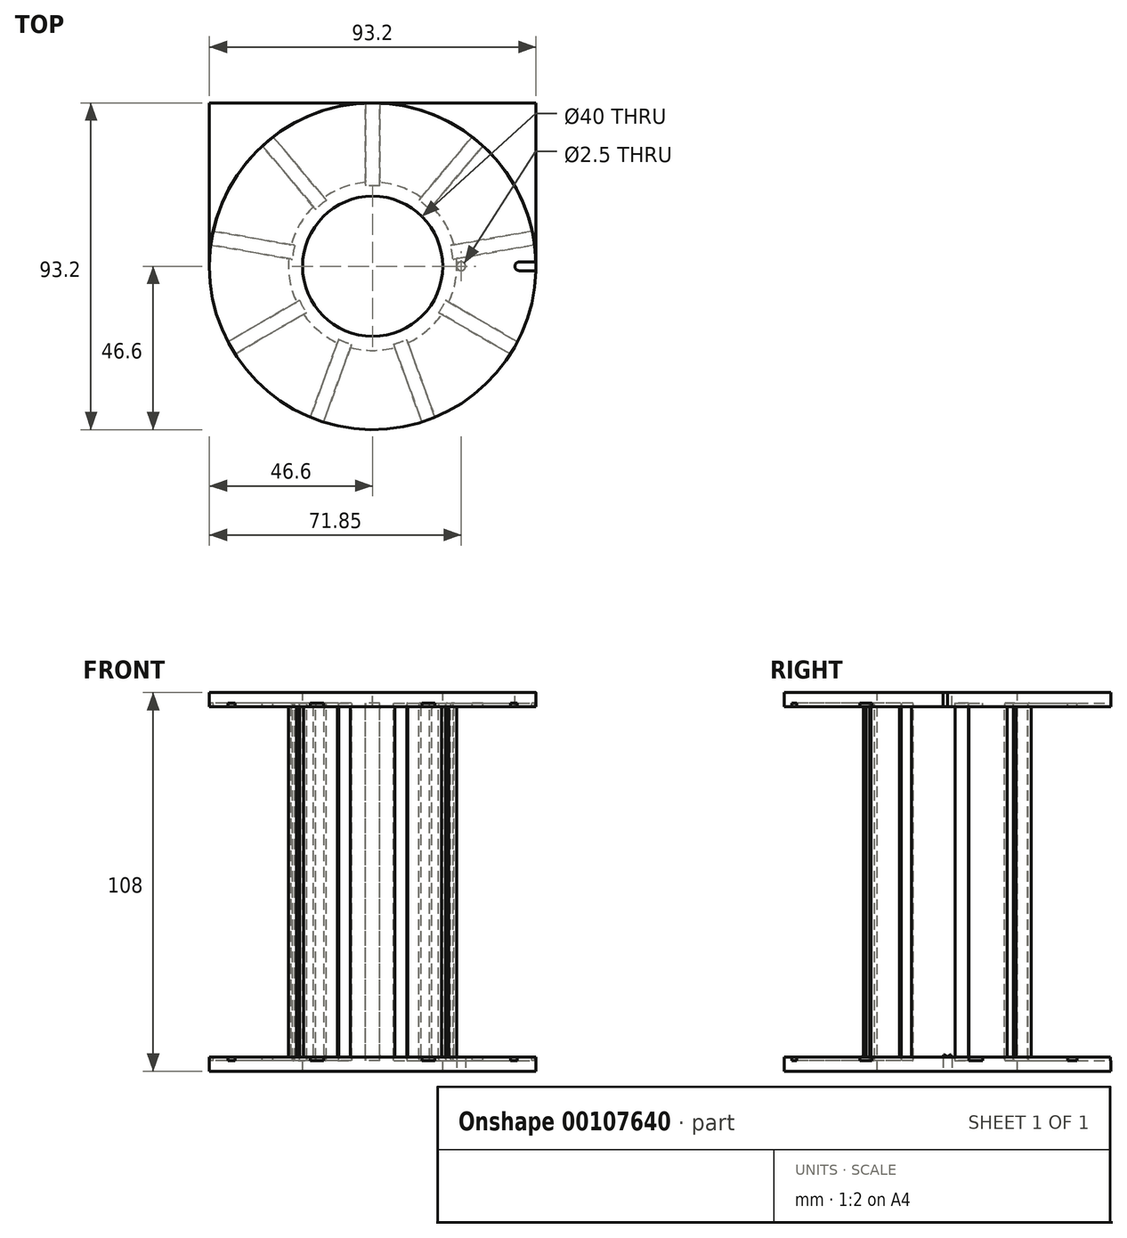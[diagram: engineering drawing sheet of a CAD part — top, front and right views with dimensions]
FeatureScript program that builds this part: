
annotation { "Feature Type Name" : "Feature", "Feature Type Description" : "" }
export const myFeature = defineFeature(function(context is Context, id is Id, definition is map)
    precondition{}
    {
        {
            assignVariable(context, id + "F0", {"name" : "t", "anyValue" : 4});
        }
        {
            assignVariable(context, id + "F1", {"name" : "w", "anyValue" : 100});
        }
        {
            var Q0;
            Q0=qCreatedBy(makeId("Front.planeOp"),FACE);
            var sketch = newSketch(context, id + "F2", { "sketchPlane" : qUnion([Q0])});
            skLineSegment(sketch, "E0.bottom", {"start": v(-46.6, 54) * mm, "end": v(-20, 54) * mm});
            skLineSegment(sketch, "E0.top", {"start": v(-46.6, -54) * mm, "end": v(-20, -54) * mm});
            skLineSegment(sketch, "E0.left", {"start": v(-46.6, 54) * mm, "end": v(-46.6, 50) * mm});
            skLineSegment(sketch, "E0.right", {"start": v(-20, 54) * mm, "end": v(-20, 1) * mm});
            skLineSegment(sketch, "E1.bottom", {"start": v(-46.6, 50) * mm, "end": v(-24, 50) * mm});
            skLineSegment(sketch, "E1.top", {"start": v(-46.6, -50) * mm, "end": v(-24, -50) * mm});
            skLineSegment(sketch, "E1.right", {"start": v(-24, 50) * mm, "end": v(-24, -50) * mm});
            skLineSegment(sketch, "E2.trimOffspring", {"start": v(-46.6, -50) * mm, "end": v(-46.6, -54) * mm});
            skPoint(sketch, "E3", {"position": v(-20, 0) * mm});
            skLineSegment(sketch, "E4", {"start": v(0, 33.62) * mm, "end": v(0, -32.3) * mm, "construction": true});
            skLineSegment(sketch, "E5", {"start": v(33.6, 0) * mm, "end": v(-41.32, 0) * mm, "construction": true});
            skLineSegment(sketch, "E6.trimOffspring", {"start": v(-20, -1) * mm, "end": v(-20, -54) * mm});
            skLineSegment(sketch, "E7", {"start": v(-20, 1) * mm, "end": v(-20, -1) * mm});
            skSolve(sketch);
        }
        {
            var Q0;
            Q0=makeQuery(id+"F2.imprint","IMPRINT",FACE,{"disambiguationData":[TD([[makeQuery(id+"F2.imprint","IMPRINT",EDGE,{"derivedFrom":sQuery(id+"F2.wireOp",EDGE,"E0.bottom")}),-1.0]])]});
            var Q1;
            Q1=sQuery(id+"F2.wireOp",EDGE,"E4");
            revolve(context, id + "F3", {"entities" : qUnion([Q0]), "axis" : qUnion([Q1]), "revolveType" : RevolveType.FULL});
        }
        {
            var Q0;
            Q0=qCreatedBy(makeId("Top.planeOp"),FACE);
            var sketch = newSketch(context, id + "F4", { "sketchPlane" : qUnion([Q0])});
            skLineSegment(sketch, "E8", {"start": v(0, 46.6) * mm, "end": v(0, 0) * mm, "construction": true});
            skLineSegment(sketch, "E9", {"start": v(0, 0) * mm, "end": v(47, 0) * mm, "construction": true});
            skLineSegment(sketch, "E10", {"start": v(0, 0) * mm, "end": v(-47, 0) * mm, "construction": true});
            skLineSegment(sketch, "E11", {"start": v(0, 0) * mm, "end": v(0, -47) * mm, "construction": true});
            skLineSegment(sketch, "E12", {"start": v(0, 46.6) * mm, "end": v(-47, 0) * mm, "construction": true});
            skLineSegment(sketch, "E13", {"start": v(0, -47) * mm, "end": v(-47, 0) * mm, "construction": true});
            skLineSegment(sketch, "E14", {"start": v(0, -47) * mm, "end": v(47, 0) * mm, "construction": true});
            skLineSegment(sketch, "E15", {"start": v(0, 46.6) * mm, "end": v(47, 0) * mm, "construction": true});
            skLineSegment(sketch, "E16", {"start": v(0, 0) * mm, "end": v(23.5, 23.3) * mm, "construction": true});
            skLineSegment(sketch, "E17", {"start": v(0, 0) * mm, "end": v(23.5, -23.5) * mm, "construction": true});
            skLineSegment(sketch, "E18", {"start": v(0, 0) * mm, "end": v(-23.5, -23.5) * mm, "construction": true});
            skLineSegment(sketch, "E19", {"start": v(0, 0) * mm, "end": v(-23.5, 23.3) * mm, "construction": true});
            skCircle(sketch, "E20", {"center": v(0, 0) * mm, "radius": 23 * mm});
            skLineSegment(sketch, "E21.bottom", {"start": v(-2, 22.91) * mm, "end": v(2, 22.91) * mm});
            skLineSegment(sketch, "E21.top", {"start": v(-2, 46.6) * mm, "end": v(2, 46.6) * mm});
            skLineSegment(sketch, "E21.left", {"start": v(-2, 22.91) * mm, "end": v(-2, 46.6) * mm});
            skLineSegment(sketch, "E21.right", {"start": v(2, 22.91) * mm, "end": v(2, 46.6) * mm});
            skLineSegment(sketch, "E22.1.0", {"start": v(16.26, 16.27) * mm, "end": v(31.49, 34.41) * mm});
            skLineSegment(sketch, "E22.1.1", {"start": v(13.2, 18.84) * mm, "end": v(28.42, 36.98) * mm});
            skLineSegment(sketch, "E22.1.2", {"start": v(28.42, 36.98) * mm, "end": v(31.49, 34.41) * mm});
            skLineSegment(sketch, "E22.2.0", {"start": v(22.91, 2) * mm, "end": v(46.24, 6.12) * mm});
            skLineSegment(sketch, "E22.2.1", {"start": v(22.22, 5.95) * mm, "end": v(45.54, 10.06) * mm});
            skLineSegment(sketch, "E22.2.2", {"start": v(45.54, 10.06) * mm, "end": v(46.24, 6.12) * mm});
            skLineSegment(sketch, "E22.3.0", {"start": v(18.84, -13.19) * mm, "end": v(39.36, -25.03) * mm});
            skLineSegment(sketch, "E22.3.1", {"start": v(20.84, -9.72) * mm, "end": v(41.36, -21.57) * mm});
            skLineSegment(sketch, "E22.3.2", {"start": v(41.36, -21.57) * mm, "end": v(39.36, -25.03) * mm});
            skLineSegment(sketch, "E22.4.0", {"start": v(5.96, -22.22) * mm, "end": v(14.06, -44.47) * mm});
            skLineSegment(sketch, "E22.4.1", {"start": v(9.72, -20.85) * mm, "end": v(17.82, -43.1) * mm});
            skLineSegment(sketch, "E22.4.2", {"start": v(17.82, -43.1) * mm, "end": v(14.06, -44.47) * mm});
            skLineSegment(sketch, "E22.5.0", {"start": v(-9.72, -20.85) * mm, "end": v(-17.82, -43.1) * mm});
            skLineSegment(sketch, "E22.5.1", {"start": v(-5.96, -22.22) * mm, "end": v(-14.06, -44.47) * mm});
            skLineSegment(sketch, "E22.5.2", {"start": v(-14.06, -44.47) * mm, "end": v(-17.82, -43.1) * mm});
            skLineSegment(sketch, "E22.anchor1", {"start": v(0, 0) * mm, "end": v(2, 22.91) * mm, "construction": true});
            skLineSegment(sketch, "E22.anchor2", {"start": v(0, 0) * mm, "end": v(2, 22.91) * mm, "construction": true});
            skLineSegment(sketch, "E23.1.6.0", {"start": v(-20.84, -9.72) * mm, "end": v(-41.36, -21.57) * mm});
            skLineSegment(sketch, "E23.3.6.0", {"start": v(-18.84, -13.19) * mm, "end": v(-39.36, -25.03) * mm});
            skLineSegment(sketch, "E23.6.6.0", {"start": v(-39.36, -25.03) * mm, "end": v(-41.36, -21.57) * mm});
            skLineSegment(sketch, "E23.1.7.0", {"start": v(-22.22, 5.95) * mm, "end": v(-45.54, 10.06) * mm});
            skLineSegment(sketch, "E23.3.7.0", {"start": v(-22.91, 2) * mm, "end": v(-46.24, 6.12) * mm});
            skLineSegment(sketch, "E23.6.7.0", {"start": v(-46.24, 6.12) * mm, "end": v(-45.54, 10.06) * mm});
            skLineSegment(sketch, "E24.1.8.0", {"start": v(-13.2, 18.84) * mm, "end": v(-28.42, 36.98) * mm});
            skLineSegment(sketch, "E24.3.8.0", {"start": v(-16.26, 16.27) * mm, "end": v(-31.49, 34.41) * mm});
            skLineSegment(sketch, "E24.6.8.0", {"start": v(-31.49, 34.41) * mm, "end": v(-28.42, 36.98) * mm});
            skSolve(sketch);
        }
        {
            var Q0;
            {var subQ0=sQuery(id+"F4.wireOp",EDGE,"E22.5.0");Q0=makeQuery(id+"F4.imprint","IMPRINT",FACE,{"disambiguationData":[TD([[makeQuery(id+"F4.imprint","IMPRINT",EDGE,{"derivedFrom":subQ0}),1.0]])]});}
            var Q1;
            Q1=makeQuery(id+"F4.imprint","IMPRINT",FACE,{"disambiguationData":[TD([[makeQuery(id+"F4.imprint","IMPRINT",EDGE,{"derivedFrom":sQuery(id+"F4.wireOp",EDGE,"E21.top")}),-1.0]])]});
            var Q2;
            {var subQ0=sQuery(id+"F4.wireOp",EDGE,"E22.1.0");Q2=makeQuery(id+"F4.imprint","IMPRINT",FACE,{"disambiguationData":[TD([[makeQuery(id+"F4.imprint","IMPRINT",EDGE,{"derivedFrom":subQ0}),1.0]])]});}
            var Q3;
            {var subQ0=sQuery(id+"F4.wireOp",EDGE,"E22.2.0");Q3=makeQuery(id+"F4.imprint","IMPRINT",FACE,{"disambiguationData":[TD([[makeQuery(id+"F4.imprint","IMPRINT",EDGE,{"derivedFrom":subQ0}),1.0]])]});}
            var Q4;
            {var subQ0=sQuery(id+"F4.wireOp",EDGE,"E22.3.0");Q4=makeQuery(id+"F4.imprint","IMPRINT",FACE,{"disambiguationData":[TD([[makeQuery(id+"F4.imprint","IMPRINT",EDGE,{"derivedFrom":subQ0}),1.0]])]});}
            var Q5;
            {var subQ0=sQuery(id+"F4.wireOp",EDGE,"E22.4.0");Q5=makeQuery(id+"F4.imprint","IMPRINT",FACE,{"disambiguationData":[TD([[makeQuery(id+"F4.imprint","IMPRINT",EDGE,{"derivedFrom":subQ0}),1.0]])]});}
            var Q6;
            {var subQ0=sQuery(id+"F4.wireOp",EDGE,"E23.1.6.0");Q6=makeQuery(id+"F4.imprint","IMPRINT",FACE,{"disambiguationData":[TD([[makeQuery(id+"F4.imprint","IMPRINT",EDGE,{"derivedFrom":subQ0}),1.0]])]});}
            var Q7;
            {var subQ3=sQuery(id+"F4.wireOp",EDGE,"E23.1.7.0");Q7=makeQuery(id+"F4.imprint","IMPRINT",FACE,{"disambiguationData":[TD([[makeQuery(id+"F4.imprint","IMPRINT",EDGE,{"derivedFrom":subQ3}),1.0]])]});}
            var Q8;
            {var subQ0=sQuery(id+"F4.wireOp",EDGE,"E24.1.8.0");Q8=makeQuery(id+"F4.imprint","IMPRINT",FACE,{"disambiguationData":[TD([[makeQuery(id+"F4.imprint","IMPRINT",EDGE,{"derivedFrom":subQ0}),1.0]])]});}
            var Q9;
            {var subQ3=sQuery(id+"F4.wireOp",EDGE,"E21.right");Q9=makeQuery(id+"F4.imprint","IMPRINT",FACE,{"disambiguationData":[TD([[makeQuery(id+"F4.imprint","IMPRINT",EDGE,{"derivedFrom":subQ3}),1.0]])]});}
            extrude(context, id + "F5", {"entities" : qUnion([Q0, Q1, Q2, Q3, Q4, Q5, Q6, Q7, Q8, Q9]), "operationType" : NewBodyOperationType.REMOVE, "endBound" : BoundingType.SYMMETRIC, "oppositeDirection" : true, "depth" : (getVariable(context, 'w') + 2 * getVariable(context, 't') - 6) * mm});
        }
        {
            var Q0;
            Q0=makeQuery(id+"F3.opRevolve","SWEPT_FACE",FACE,{"disambiguationData":[OSD([sQuery(id+"F2.wireOp",EDGE,"E0.bottom")])]});
            var sketch = newSketch(context, id + "F6", { "sketchPlane" : qUnion([Q0])});
            skLineSegment(sketch, "E25", {"start": v(-46.6, 0) * mm, "end": v(46.6, 0) * mm, "construction": true});
            skLineSegment(sketch, "E26", {"start": v(0, 46.6) * mm, "end": v(0, -46.6) * mm, "construction": true});
            skLineSegment(sketch, "E27.bottom", {"start": v(46.6, 1.25) * mm, "end": v(41.85, 1.25) * mm});
            skLineSegment(sketch, "E27.top", {"start": v(46.6, -1.25) * mm, "end": v(41.85, -1.25) * mm});
            skLineSegment(sketch, "E27.left", {"start": v(46.6, 1.25) * mm, "end": v(46.6, -1.25) * mm});
            skLineSegment(sketch, "E27.right", {"start": v(40.6, 0) * mm, "end": v(40.6, 0) * mm});
            skPoint(sketch, "E28", {"position": v(46.6, 0) * mm});
            skPoint(sketch, "E29.visualSharp", {"position": v(40.6, -1.25) * mm});
            skArc(sketch, "E29.filletArc", {"start": v(40.6, 0) * mm, "mid": v(40.97, -0.88) * mm, "end": v(41.85, -1.25) * mm});
            skPoint(sketch, "E30.visualSharp", {"position": v(40.6, 1.25) * mm});
            skArc(sketch, "E30.filletArc", {"start": v(41.85, 1.25) * mm, "mid": v(40.97, 0.88) * mm, "end": v(40.6, 0) * mm});
            skSolve(sketch);
        }
        {
            var Q0;
            {var subQ1=sQuery(id+"F6.wireOp",EDGE,"E29.filletArc");Q0=makeQuery(id+"F6.imprint","IMPRINT",FACE,{"disambiguationData":[TD([[makeQuery(id+"F6.imprint","IMPRINT",EDGE,{"derivedFrom":subQ1}),1.0]])]});}
            var Q1;
            Q1=makeQuery(id+"F5.boolean.opBoolean","SPLIT",FACE,{"disambiguationData":[TD([makeQuery(id+"F5.opExtrude","SWEPT_FACE",FACE,{"disambiguationData":[OSD([sQuery(id+"F4.wireOp",EDGE,"E22.1.0")])]})])],"derivedFrom":makeQuery(id+"F3.opRevolve","SWEPT_FACE",FACE,{"disambiguationData":[OSD([sQuery(id+"F2.wireOp",EDGE,"E1.bottom")])]})});
            extrude(context, id + "F7", {"entities" : qUnion([Q0]), "operationType" : NewBodyOperationType.REMOVE, "endBound" : BoundingType.UP_TO_SURFACE, "oppositeDirection" : true, "endBoundEntityFace" : qUnion([Q1]), "depth" : 25 * mm});
        }
        {
            var Q0;
            Q0=makeQuery(id+"F3.opRevolve","SWEPT_FACE",FACE,{"disambiguationData":[OSD([sQuery(id+"F2.wireOp",EDGE,"E0.top")])]});
            var sketch = newSketch(context, id + "F8", { "sketchPlane" : qUnion([Q0])});
            skLineSegment(sketch, "E31", {"start": v(0, 0) * mm, "end": v(9.84, 0) * mm, "construction": true});
            skCircle(sketch, "E32", {"center": v(25.25, 0) * mm, "radius": 1.25 * mm});
            skSolve(sketch);
        }
        {
            var Q0;
            Q0=makeQuery(id+"F8.imprint","IMPRINT",FACE,{"disambiguationData":[TD([[makeQuery(id+"F8.imprint","IMPRINT",EDGE,{"derivedFrom":sQuery(id+"F8.wireOp",EDGE,"E32")}),1.0]])]});
            var Q1;
            Q1=makeQuery(id+"F5.boolean.opBoolean","SPLIT",FACE,{"disambiguationData":[TD([makeQuery(id+"F5.opExtrude","SWEPT_FACE",FACE,{"disambiguationData":[OSD([sQuery(id+"F4.wireOp",EDGE,"E22.1.0")])]})])],"derivedFrom":makeQuery(id+"F3.opRevolve","SWEPT_FACE",FACE,{"disambiguationData":[OSD([sQuery(id+"F2.wireOp",EDGE,"E1.top")])]})});
            extrude(context, id + "F9", {"entities" : qUnion([Q0]), "operationType" : NewBodyOperationType.REMOVE, "endBound" : BoundingType.UP_TO_SURFACE, "oppositeDirection" : true, "endBoundEntityFace" : qUnion([Q1]), "depth" : 25 * mm});
        }
        {
            var Q0;
            {var subQ0=sQuery(id+"F2.wireOp",EDGE,"E1.top");var subQ2=makeQuery(id+"F5.opExtrude","SWEPT_FACE",FACE,{"disambiguationData":[OSD([sQuery(id+"F4.wireOp",EDGE,"E22.3.1")])]});var subQ3=sQuery(id+"F2.wireOp",EDGE,"E1.right");Q0=makeQuery(id+"F9.boolean.opBoolean","SPLIT",EDGE,{"disambiguationData":[TD([makeQuery(id+"F5.boolean.opBoolean","COPY",FACE,{"derivedFrom":subQ2})])],"derivedFrom":makeQuery(id+"F5.boolean.opBoolean","SPLIT",EDGE,{"disambiguationData":[TD([makeQuery(id+"F5.opExtrude","SWEPT_FACE",FACE,{"disambiguationData":[OSD([sQuery(id+"F4.wireOp",EDGE,"E22.2.0")])]})])],"derivedFrom":makeQuery(id+"F3.opRevolve","SWEPT_EDGE",EDGE,{"disambiguationData":[OSD([subQ0,subQ3])]})})});}
            var Q1;
            {var subQ0=sQuery(id+"F2.wireOp",EDGE,"E1.top");var subQ1=sQuery(id+"F2.wireOp",EDGE,"E1.right");Q1=makeQuery(id+"F5.boolean.opBoolean","SPLIT",EDGE,{"disambiguationData":[TD([makeQuery(id+"F5.opExtrude","SWEPT_FACE",FACE,{"disambiguationData":[OSD([sQuery(id+"F4.wireOp",EDGE,"E22.3.0")])]})])],"derivedFrom":makeQuery(id+"F3.opRevolve","SWEPT_EDGE",EDGE,{"disambiguationData":[OSD([subQ0,subQ1])]})});}
            var Q2;
            {var subQ0=sQuery(id+"F2.wireOp",EDGE,"E1.top");var subQ1=sQuery(id+"F2.wireOp",EDGE,"E1.right");Q2=makeQuery(id+"F5.boolean.opBoolean","SPLIT",EDGE,{"disambiguationData":[TD([makeQuery(id+"F5.opExtrude","SWEPT_FACE",FACE,{"disambiguationData":[OSD([sQuery(id+"F4.wireOp",EDGE,"E22.4.0")])]})])],"derivedFrom":makeQuery(id+"F3.opRevolve","SWEPT_EDGE",EDGE,{"disambiguationData":[OSD([subQ0,subQ1])]})});}
            var Q3;
            {var subQ0=sQuery(id+"F2.wireOp",EDGE,"E1.top");var subQ1=sQuery(id+"F2.wireOp",EDGE,"E1.right");Q3=makeQuery(id+"F5.boolean.opBoolean","SPLIT",EDGE,{"disambiguationData":[TD([makeQuery(id+"F5.opExtrude","SWEPT_FACE",FACE,{"disambiguationData":[OSD([sQuery(id+"F4.wireOp",EDGE,"E22.1.0")])]})])],"derivedFrom":makeQuery(id+"F3.opRevolve","SWEPT_EDGE",EDGE,{"disambiguationData":[OSD([subQ0,subQ1])]})});}
            var Q4;
            {var subQ0=sQuery(id+"F2.wireOp",EDGE,"E1.top");var subQ1=sQuery(id+"F2.wireOp",EDGE,"E1.right");Q4=makeQuery(id+"F5.boolean.opBoolean","SPLIT",EDGE,{"disambiguationData":[TD([makeQuery(id+"F5.opExtrude","SWEPT_FACE",FACE,{"disambiguationData":[OSD([sQuery(id+"F4.wireOp",EDGE,"E22.1.1")])]})])],"derivedFrom":makeQuery(id+"F3.opRevolve","SWEPT_EDGE",EDGE,{"disambiguationData":[OSD([subQ0,subQ1])]})});}
            var Q5;
            {var subQ0=sQuery(id+"F2.wireOp",EDGE,"E1.top");var subQ1=sQuery(id+"F2.wireOp",EDGE,"E1.right");Q5=makeQuery(id+"F5.boolean.opBoolean","SPLIT",EDGE,{"disambiguationData":[TD([makeQuery(id+"F5.opExtrude","SWEPT_FACE",FACE,{"disambiguationData":[OSD([sQuery(id+"F4.wireOp",EDGE,"E24.1.8.0")])]})])],"derivedFrom":makeQuery(id+"F3.opRevolve","SWEPT_EDGE",EDGE,{"disambiguationData":[OSD([subQ0,subQ1])]})});}
            var Q6;
            {var subQ0=sQuery(id+"F2.wireOp",EDGE,"E1.top");var subQ1=sQuery(id+"F2.wireOp",EDGE,"E1.right");Q6=makeQuery(id+"F5.boolean.opBoolean","SPLIT",EDGE,{"disambiguationData":[TD([makeQuery(id+"F5.opExtrude","SWEPT_FACE",FACE,{"disambiguationData":[OSD([sQuery(id+"F4.wireOp",EDGE,"E23.1.7.0")])]})])],"derivedFrom":makeQuery(id+"F3.opRevolve","SWEPT_EDGE",EDGE,{"disambiguationData":[OSD([subQ0,subQ1])]})});}
            var Q7;
            {var subQ0=sQuery(id+"F2.wireOp",EDGE,"E1.top");var subQ1=sQuery(id+"F2.wireOp",EDGE,"E1.right");Q7=makeQuery(id+"F5.boolean.opBoolean","SPLIT",EDGE,{"disambiguationData":[TD([makeQuery(id+"F5.opExtrude","SWEPT_FACE",FACE,{"disambiguationData":[OSD([sQuery(id+"F4.wireOp",EDGE,"E22.5.0")])]})])],"derivedFrom":makeQuery(id+"F3.opRevolve","SWEPT_EDGE",EDGE,{"disambiguationData":[OSD([subQ0,subQ1])]})});}
            var Q8;
            {var subQ0=sQuery(id+"F2.wireOp",EDGE,"E1.top");var subQ1=sQuery(id+"F2.wireOp",EDGE,"E1.right");Q8=makeQuery(id+"F5.boolean.opBoolean","SPLIT",EDGE,{"disambiguationData":[TD([makeQuery(id+"F5.opExtrude","SWEPT_FACE",FACE,{"disambiguationData":[OSD([sQuery(id+"F4.wireOp",EDGE,"E23.1.6.0")])]})])],"derivedFrom":makeQuery(id+"F3.opRevolve","SWEPT_EDGE",EDGE,{"disambiguationData":[OSD([subQ0,subQ1])]})});}
            var Q9;
            {var subQ0=sQuery(id+"F2.wireOp",EDGE,"E1.bottom");var subQ1=sQuery(id+"F2.wireOp",EDGE,"E1.right");Q9=makeQuery(id+"F5.boolean.opBoolean","SPLIT",EDGE,{"disambiguationData":[TD([makeQuery(id+"F5.opExtrude","SWEPT_FACE",FACE,{"disambiguationData":[OSD([sQuery(id+"F4.wireOp",EDGE,"E22.5.0")])]})])],"derivedFrom":makeQuery(id+"F3.opRevolve","SWEPT_EDGE",EDGE,{"disambiguationData":[OSD([subQ0,subQ1])]})});}
            var Q10;
            {var subQ0=sQuery(id+"F2.wireOp",EDGE,"E1.bottom");var subQ1=sQuery(id+"F2.wireOp",EDGE,"E1.right");Q10=makeQuery(id+"F5.boolean.opBoolean","SPLIT",EDGE,{"disambiguationData":[TD([makeQuery(id+"F5.opExtrude","SWEPT_FACE",FACE,{"disambiguationData":[OSD([sQuery(id+"F4.wireOp",EDGE,"E23.1.6.0")])]})])],"derivedFrom":makeQuery(id+"F3.opRevolve","SWEPT_EDGE",EDGE,{"disambiguationData":[OSD([subQ0,subQ1])]})});}
            var Q11;
            {var subQ0=sQuery(id+"F2.wireOp",EDGE,"E1.bottom");var subQ1=sQuery(id+"F2.wireOp",EDGE,"E1.right");Q11=makeQuery(id+"F5.boolean.opBoolean","SPLIT",EDGE,{"disambiguationData":[TD([makeQuery(id+"F5.opExtrude","SWEPT_FACE",FACE,{"disambiguationData":[OSD([sQuery(id+"F4.wireOp",EDGE,"E22.4.0")])]})])],"derivedFrom":makeQuery(id+"F3.opRevolve","SWEPT_EDGE",EDGE,{"disambiguationData":[OSD([subQ0,subQ1])]})});}
            var Q12;
            {var subQ0=sQuery(id+"F2.wireOp",EDGE,"E1.bottom");var subQ1=sQuery(id+"F2.wireOp",EDGE,"E1.right");Q12=makeQuery(id+"F5.boolean.opBoolean","SPLIT",EDGE,{"disambiguationData":[TD([makeQuery(id+"F5.opExtrude","SWEPT_FACE",FACE,{"disambiguationData":[OSD([sQuery(id+"F4.wireOp",EDGE,"E22.3.0")])]})])],"derivedFrom":makeQuery(id+"F3.opRevolve","SWEPT_EDGE",EDGE,{"disambiguationData":[OSD([subQ0,subQ1])]})});}
            var Q13;
            {var subQ0=sQuery(id+"F2.wireOp",EDGE,"E1.bottom");var subQ1=sQuery(id+"F2.wireOp",EDGE,"E1.right");Q13=makeQuery(id+"F5.boolean.opBoolean","SPLIT",EDGE,{"disambiguationData":[TD([makeQuery(id+"F5.opExtrude","SWEPT_FACE",FACE,{"disambiguationData":[OSD([sQuery(id+"F4.wireOp",EDGE,"E22.2.0")])]})])],"derivedFrom":makeQuery(id+"F3.opRevolve","SWEPT_EDGE",EDGE,{"disambiguationData":[OSD([subQ0,subQ1])]})});}
            var Q14;
            {var subQ0=sQuery(id+"F2.wireOp",EDGE,"E1.bottom");var subQ1=sQuery(id+"F2.wireOp",EDGE,"E1.right");Q14=makeQuery(id+"F5.boolean.opBoolean","SPLIT",EDGE,{"disambiguationData":[TD([makeQuery(id+"F5.opExtrude","SWEPT_FACE",FACE,{"disambiguationData":[OSD([sQuery(id+"F4.wireOp",EDGE,"E22.1.0")])]})])],"derivedFrom":makeQuery(id+"F3.opRevolve","SWEPT_EDGE",EDGE,{"disambiguationData":[OSD([subQ0,subQ1])]})});}
            var Q15;
            {var subQ0=sQuery(id+"F2.wireOp",EDGE,"E1.bottom");var subQ1=sQuery(id+"F2.wireOp",EDGE,"E1.right");Q15=makeQuery(id+"F5.boolean.opBoolean","SPLIT",EDGE,{"disambiguationData":[TD([makeQuery(id+"F5.opExtrude","SWEPT_FACE",FACE,{"disambiguationData":[OSD([sQuery(id+"F4.wireOp",EDGE,"E22.1.1")])]})])],"derivedFrom":makeQuery(id+"F3.opRevolve","SWEPT_EDGE",EDGE,{"disambiguationData":[OSD([subQ0,subQ1])]})});}
            var Q16;
            {var subQ0=sQuery(id+"F2.wireOp",EDGE,"E1.bottom");var subQ1=sQuery(id+"F2.wireOp",EDGE,"E1.right");Q16=makeQuery(id+"F5.boolean.opBoolean","SPLIT",EDGE,{"disambiguationData":[TD([makeQuery(id+"F5.opExtrude","SWEPT_FACE",FACE,{"disambiguationData":[OSD([sQuery(id+"F4.wireOp",EDGE,"E24.1.8.0")])]})])],"derivedFrom":makeQuery(id+"F3.opRevolve","SWEPT_EDGE",EDGE,{"disambiguationData":[OSD([subQ0,subQ1])]})});}
            var Q17;
            {var subQ0=sQuery(id+"F2.wireOp",EDGE,"E1.bottom");var subQ1=sQuery(id+"F2.wireOp",EDGE,"E1.right");Q17=makeQuery(id+"F5.boolean.opBoolean","SPLIT",EDGE,{"disambiguationData":[TD([makeQuery(id+"F5.opExtrude","SWEPT_FACE",FACE,{"disambiguationData":[OSD([sQuery(id+"F4.wireOp",EDGE,"E23.1.7.0")])]})])],"derivedFrom":makeQuery(id+"F3.opRevolve","SWEPT_EDGE",EDGE,{"disambiguationData":[OSD([subQ0,subQ1])]})});}
            fillet(context, id + "F10", {"entities" : qUnion([Q0, Q1, Q2, Q3, Q4, Q5, Q6, Q7, Q8, Q9, Q10, Q11, Q12, Q13, Q14, Q15, Q16, Q17]), "radius" : (1.41 / 2) * mm, "tangentPropagation" : true, "allowEdgeOverflow" : false});
        }
        {
            var Q0;
            {var subQ0=sQuery(id+"F4.wireOp",EDGE,"E20");Q0=makeQuery(id+"F5.boolean.opBoolean","COPY",EDGE,{"derivedFrom":makeQuery(id+"F5.opExtrude","CAP_EDGE",EDGE,{"disambiguationData":[OSD([subQ0]),TDD([makeQuery(id+"F4.imprint","IMPRINT",EDGE,{"disambiguationData":[TD([[makeQuery(id+"F4.imprint","INTERSECT",VERTEX,{"derivedFrom":[subQ0,sQuery(id+"F4.wireOp",EDGE,"E22.4.0")]}),-1.0]])],"derivedFrom":subQ0})])],"isStart":false})});}
            var Q1;
            {var subQ0=sQuery(id+"F4.wireOp",EDGE,"E20");Q1=makeQuery(id+"F5.boolean.opBoolean","COPY",EDGE,{"derivedFrom":makeQuery(id+"F5.opExtrude","CAP_EDGE",EDGE,{"disambiguationData":[OSD([subQ0]),TDD([makeQuery(id+"F4.imprint","IMPRINT",EDGE,{"disambiguationData":[TD([[makeQuery(id+"F4.imprint","INTERSECT",VERTEX,{"derivedFrom":[subQ0,sQuery(id+"F4.wireOp",EDGE,"E22.3.0")]}),-1.0]])],"derivedFrom":subQ0})])],"isStart":false})});}
            var Q2;
            {var subQ0=sQuery(id+"F4.wireOp",EDGE,"E20");Q2=makeQuery(id+"F5.boolean.opBoolean","COPY",EDGE,{"derivedFrom":makeQuery(id+"F5.opExtrude","CAP_EDGE",EDGE,{"disambiguationData":[OSD([subQ0]),TDD([makeQuery(id+"F4.imprint","IMPRINT",EDGE,{"disambiguationData":[TD([[makeQuery(id+"F4.imprint","INTERSECT",VERTEX,{"derivedFrom":[subQ0,sQuery(id+"F4.wireOp",EDGE,"E22.5.0")]}),-1.0]])],"derivedFrom":subQ0})])],"isStart":false})});}
            var Q3;
            {var subQ0=sQuery(id+"F4.wireOp",EDGE,"E20");Q3=makeQuery(id+"F5.boolean.opBoolean","COPY",EDGE,{"derivedFrom":makeQuery(id+"F5.opExtrude","CAP_EDGE",EDGE,{"disambiguationData":[OSD([subQ0]),TDD([makeQuery(id+"F4.imprint","IMPRINT",EDGE,{"disambiguationData":[TD([[makeQuery(id+"F4.imprint","INTERSECT",VERTEX,{"derivedFrom":[subQ0,sQuery(id+"F4.wireOp",EDGE,"E22.2.0")]}),-1.0]])],"derivedFrom":subQ0})])],"isStart":false})});}
            var Q4;
            {var subQ0=sQuery(id+"F4.wireOp",EDGE,"E20");Q4=makeQuery(id+"F5.boolean.opBoolean","COPY",EDGE,{"derivedFrom":makeQuery(id+"F5.opExtrude","CAP_EDGE",EDGE,{"disambiguationData":[OSD([subQ0]),TDD([makeQuery(id+"F4.imprint","IMPRINT",EDGE,{"disambiguationData":[TD([[makeQuery(id+"F4.imprint","INTERSECT",VERTEX,{"derivedFrom":[subQ0,sQuery(id+"F4.wireOp",EDGE,"E22.1.0")]}),-1.0]])],"derivedFrom":subQ0})])],"isStart":false})});}
            var Q5;
            {var subQ0=sQuery(id+"F4.wireOp",EDGE,"E21.bottom");var subQ1=sQuery(id+"F4.wireOp",EDGE,"E20");Q5=makeQuery(id+"F5.boolean.opBoolean","COPY",EDGE,{"derivedFrom":makeQuery(id+"F5.opExtrude","CAP_EDGE",EDGE,{"disambiguationData":[OSD([subQ1]),TDD([makeQuery(id+"F4.imprint","IMPRINT",EDGE,{"disambiguationData":[TD([[makeQuery(id+"F4.imprint","INTERSECT",VERTEX,{"derivedFrom":[subQ1,subQ0,sQuery(id+"F4.wireOp",EDGE,"E21.left")]}),1.0]])],"derivedFrom":subQ1})])],"isStart":false})});}
            var Q6;
            {var subQ0=sQuery(id+"F4.wireOp",EDGE,"E20");Q6=makeQuery(id+"F5.boolean.opBoolean","COPY",EDGE,{"derivedFrom":makeQuery(id+"F5.opExtrude","CAP_EDGE",EDGE,{"disambiguationData":[OSD([subQ0]),TDD([makeQuery(id+"F4.imprint","IMPRINT",EDGE,{"disambiguationData":[TD([[makeQuery(id+"F4.imprint","INTERSECT",VERTEX,{"derivedFrom":[subQ0,sQuery(id+"F4.wireOp",EDGE,"E24.1.8.0")]}),-1.0]])],"derivedFrom":subQ0})])],"isStart":false})});}
            var Q7;
            {var subQ0=sQuery(id+"F4.wireOp",EDGE,"E20");Q7=makeQuery(id+"F5.boolean.opBoolean","COPY",EDGE,{"derivedFrom":makeQuery(id+"F5.opExtrude","CAP_EDGE",EDGE,{"disambiguationData":[OSD([subQ0]),TDD([makeQuery(id+"F4.imprint","IMPRINT",EDGE,{"disambiguationData":[TD([[makeQuery(id+"F4.imprint","INTERSECT",VERTEX,{"derivedFrom":[subQ0,sQuery(id+"F4.wireOp",EDGE,"E23.1.7.0")]}),-1.0]])],"derivedFrom":subQ0})])],"isStart":false})});}
            var Q8;
            {var subQ0=sQuery(id+"F4.wireOp",EDGE,"E20");Q8=makeQuery(id+"F5.boolean.opBoolean","COPY",EDGE,{"derivedFrom":makeQuery(id+"F5.opExtrude","CAP_EDGE",EDGE,{"disambiguationData":[OSD([subQ0]),TDD([makeQuery(id+"F4.imprint","IMPRINT",EDGE,{"disambiguationData":[TD([[makeQuery(id+"F4.imprint","INTERSECT",VERTEX,{"derivedFrom":[subQ0,sQuery(id+"F4.wireOp",EDGE,"E23.1.6.0")]}),-1.0]])],"derivedFrom":subQ0})])],"isStart":false})});}
            var Q9;
            {var subQ0=sQuery(id+"F4.wireOp",EDGE,"E20");Q9=makeQuery(id+"F5.boolean.opBoolean","COPY",EDGE,{"derivedFrom":makeQuery(id+"F5.opExtrude","CAP_EDGE",EDGE,{"disambiguationData":[OSD([subQ0]),TDD([makeQuery(id+"F4.imprint","IMPRINT",EDGE,{"disambiguationData":[TD([[makeQuery(id+"F4.imprint","INTERSECT",VERTEX,{"derivedFrom":[subQ0,sQuery(id+"F4.wireOp",EDGE,"E23.1.6.0")]}),-1.0]])],"derivedFrom":subQ0})])],"isStart":true})});}
            var Q10;
            {var subQ0=sQuery(id+"F4.wireOp",EDGE,"E20");Q10=makeQuery(id+"F5.boolean.opBoolean","COPY",EDGE,{"derivedFrom":makeQuery(id+"F5.opExtrude","CAP_EDGE",EDGE,{"disambiguationData":[OSD([subQ0]),TDD([makeQuery(id+"F4.imprint","IMPRINT",EDGE,{"disambiguationData":[TD([[makeQuery(id+"F4.imprint","INTERSECT",VERTEX,{"derivedFrom":[subQ0,sQuery(id+"F4.wireOp",EDGE,"E23.1.7.0")]}),-1.0]])],"derivedFrom":subQ0})])],"isStart":true})});}
            var Q11;
            {var subQ0=sQuery(id+"F4.wireOp",EDGE,"E20");Q11=makeQuery(id+"F5.boolean.opBoolean","COPY",EDGE,{"derivedFrom":makeQuery(id+"F5.opExtrude","CAP_EDGE",EDGE,{"disambiguationData":[OSD([subQ0]),TDD([makeQuery(id+"F4.imprint","IMPRINT",EDGE,{"disambiguationData":[TD([[makeQuery(id+"F4.imprint","INTERSECT",VERTEX,{"derivedFrom":[subQ0,sQuery(id+"F4.wireOp",EDGE,"E22.5.0")]}),-1.0]])],"derivedFrom":subQ0})])],"isStart":true})});}
            var Q12;
            {var subQ0=sQuery(id+"F4.wireOp",EDGE,"E20");Q12=makeQuery(id+"F5.boolean.opBoolean","COPY",EDGE,{"derivedFrom":makeQuery(id+"F5.opExtrude","CAP_EDGE",EDGE,{"disambiguationData":[OSD([subQ0]),TDD([makeQuery(id+"F4.imprint","IMPRINT",EDGE,{"disambiguationData":[TD([[makeQuery(id+"F4.imprint","INTERSECT",VERTEX,{"derivedFrom":[subQ0,sQuery(id+"F4.wireOp",EDGE,"E22.4.0")]}),-1.0]])],"derivedFrom":subQ0})])],"isStart":true})});}
            var Q13;
            {var subQ0=sQuery(id+"F4.wireOp",EDGE,"E20");Q13=makeQuery(id+"F5.boolean.opBoolean","COPY",EDGE,{"derivedFrom":makeQuery(id+"F5.opExtrude","CAP_EDGE",EDGE,{"disambiguationData":[OSD([subQ0]),TDD([makeQuery(id+"F4.imprint","IMPRINT",EDGE,{"disambiguationData":[TD([[makeQuery(id+"F4.imprint","INTERSECT",VERTEX,{"derivedFrom":[subQ0,sQuery(id+"F4.wireOp",EDGE,"E22.3.0")]}),-1.0]])],"derivedFrom":subQ0})])],"isStart":true})});}
            var Q14;
            {var subQ0=sQuery(id+"F4.wireOp",EDGE,"E20");Q14=makeQuery(id+"F5.boolean.opBoolean","COPY",EDGE,{"derivedFrom":makeQuery(id+"F5.opExtrude","CAP_EDGE",EDGE,{"disambiguationData":[OSD([subQ0]),TDD([makeQuery(id+"F4.imprint","IMPRINT",EDGE,{"disambiguationData":[TD([[makeQuery(id+"F4.imprint","INTERSECT",VERTEX,{"derivedFrom":[subQ0,sQuery(id+"F4.wireOp",EDGE,"E22.2.0")]}),-1.0]])],"derivedFrom":subQ0})])],"isStart":true})});}
            var Q15;
            {var subQ0=sQuery(id+"F4.wireOp",EDGE,"E20");Q15=makeQuery(id+"F5.boolean.opBoolean","COPY",EDGE,{"derivedFrom":makeQuery(id+"F5.opExtrude","CAP_EDGE",EDGE,{"disambiguationData":[OSD([subQ0]),TDD([makeQuery(id+"F4.imprint","IMPRINT",EDGE,{"disambiguationData":[TD([[makeQuery(id+"F4.imprint","INTERSECT",VERTEX,{"derivedFrom":[subQ0,sQuery(id+"F4.wireOp",EDGE,"E22.1.0")]}),-1.0]])],"derivedFrom":subQ0})])],"isStart":true})});}
            var Q16;
            {var subQ0=sQuery(id+"F4.wireOp",EDGE,"E21.bottom");var subQ1=sQuery(id+"F4.wireOp",EDGE,"E20");Q16=makeQuery(id+"F5.boolean.opBoolean","COPY",EDGE,{"derivedFrom":makeQuery(id+"F5.opExtrude","CAP_EDGE",EDGE,{"disambiguationData":[OSD([subQ1]),TDD([makeQuery(id+"F4.imprint","IMPRINT",EDGE,{"disambiguationData":[TD([[makeQuery(id+"F4.imprint","INTERSECT",VERTEX,{"derivedFrom":[subQ1,subQ0,sQuery(id+"F4.wireOp",EDGE,"E21.left")]}),1.0]])],"derivedFrom":subQ1})])],"isStart":true})});}
            var Q17;
            {var subQ0=sQuery(id+"F4.wireOp",EDGE,"E20");Q17=makeQuery(id+"F5.boolean.opBoolean","COPY",EDGE,{"derivedFrom":makeQuery(id+"F5.opExtrude","CAP_EDGE",EDGE,{"disambiguationData":[OSD([subQ0]),TDD([makeQuery(id+"F4.imprint","IMPRINT",EDGE,{"disambiguationData":[TD([[makeQuery(id+"F4.imprint","INTERSECT",VERTEX,{"derivedFrom":[subQ0,sQuery(id+"F4.wireOp",EDGE,"E24.1.8.0")]}),-1.0]])],"derivedFrom":subQ0})])],"isStart":true})});}
            fillet(context, id + "F11", {"entities" : qUnion([Q0, Q1, Q2, Q3, Q4, Q5, Q6, Q7, Q8, Q9, Q10, Q11, Q12, Q13, Q14, Q15, Q16, Q17]), "radius" : .5 * mm, "tangentPropagation" : true, "allowEdgeOverflow" : false});
        }
        {
            var Q0;
            Q0=qCreatedBy(makeId("Top.planeOp"),FACE);
            var sketch = newSketch(context, id + "F12", { "sketchPlane" : qUnion([Q0])});
            skCircle(sketch, "E33", {"center": v(0, 0) * mm, "radius": 46.6 * mm});
            skLineSegment(sketch, "E34", {"start": v(-46.6, 0) * mm, "end": v(-46.6, 46.6) * mm});
            skLineSegment(sketch, "E35", {"start": v(-46.6, 46.6) * mm, "end": v(46.6, 46.6) * mm});
            skLineSegment(sketch, "E36", {"start": v(46.6, 0) * mm, "end": v(46.6, 46.6) * mm});
            skSolve(sketch);
        }
        {
            var Q0;
            Q0=makeQuery(id+"F3.opRevolve","SWEPT_FACE",FACE,{"disambiguationData":[OSD([sQuery(id+"F2.wireOp",EDGE,"E0.bottom")])]});
            var sketch = newSketch(context, id + "F13", { "sketchPlane" : qUnion([Q0])});
            skCircle(sketch, "E37", {"center": v(0, 0) * mm, "radius": 46.6 * mm});
            skLineSegment(sketch, "E38", {"start": v(-46.6, 0) * mm, "end": v(-46.6, 46.6) * mm});
            skLineSegment(sketch, "E39", {"start": v(-46.6, 46.6) * mm, "end": v(46.6, 46.6) * mm});
            skLineSegment(sketch, "E40", {"start": v(46.6, 0) * mm, "end": v(46.6, 46.6) * mm});
            skSolve(sketch);
        }
        {
            var Q0;
            {var subQ2=sQuery(id+"F13.wireOp",EDGE,"E40");Q0=makeQuery(id+"F13.imprint","IMPRINT",FACE,{"disambiguationData":[TD([[makeQuery(id+"F13.imprint","IMPRINT",EDGE,{"derivedFrom":subQ2}),1.0]])]});}
            var Q1;
            {var subQ0=sQuery(id+"F13.wireOp",EDGE,"E38");Q1=makeQuery(id+"F13.imprint","IMPRINT",FACE,{"disambiguationData":[TD([[makeQuery(id+"F13.imprint","IMPRINT",EDGE,{"derivedFrom":subQ0}),-1.0]])]});}
            extrude(context, id + "F14", {"entities" : qUnion([Q0, Q1]), "oppositeDirection" : true, "depth" : (getVariable(context, 't')) * mm});
        }
    });
